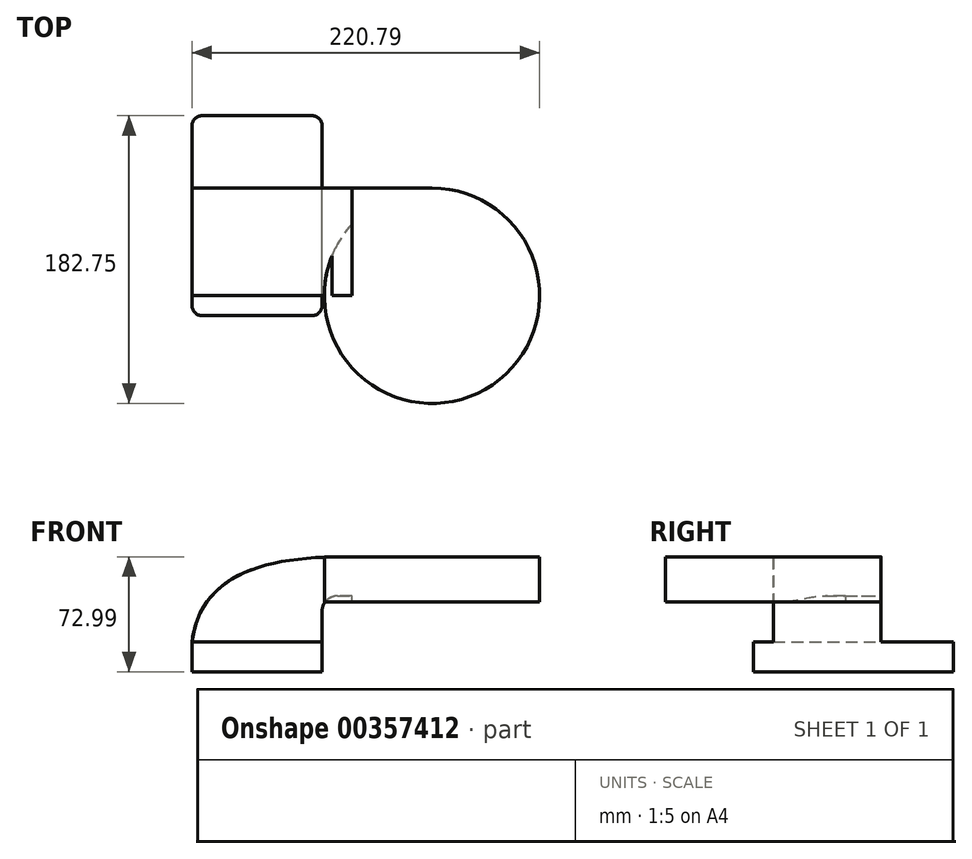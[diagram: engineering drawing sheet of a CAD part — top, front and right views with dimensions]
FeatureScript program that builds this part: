
annotation { "Feature Type Name" : "Feature", "Feature Type Description" : "" }
export const myFeature = defineFeature(function(context is Context, id is Id, definition is map)
    precondition{}
    {
        {
            var Q0;
            Q0=qCreatedBy(makeId("Front.planeOp"),FACE);
            var sketch = newSketch(context, id + "F0", { "sketchPlane" : qUnion([Q0])});
            skLineSegment(sketch, "E0.bottom", {"start": v(41.28, -9.52) * mm, "end": v(-41.28, -9.53) * mm});
            skLineSegment(sketch, "E0.top", {"start": v(41.28, 9.53) * mm, "end": v(-41.28, 9.53) * mm});
            skLineSegment(sketch, "E0.left", {"start": v(41.28, -9.52) * mm, "end": v(41.28, 9.53) * mm});
            skLineSegment(sketch, "E0.right", {"start": v(-41.28, -9.53) * mm, "end": v(-41.28, 9.53) * mm});
            skPoint(sketch, "E0.middle", {"position": v(0, 0) * mm});
            skLineSegment(sketch, "E1.bottom", {"start": v(60.33, 34.82) * mm, "end": v(111.12, 34.82) * mm});
            skLineSegment(sketch, "E1.top", {"start": v(60.33, 63.4) * mm, "end": v(111.12, 63.4) * mm});
            skLineSegment(sketch, "E1.left", {"start": v(60.33, 34.82) * mm, "end": v(60.33, 63.4) * mm});
            skLineSegment(sketch, "E1.right", {"start": v(111.12, 34.82) * mm, "end": v(111.12, 63.4) * mm});
            skPoint(sketch, "E1.middle", {"position": v(85.72, 49.11) * mm});
            skLineSegment(sketch, "E2", {"start": v(41.28, 9.53) * mm, "end": v(41.28, 28.87) * mm});
            skArc(sketch, "E3", {"start": v(41.28, 28.87) * mm, "mid": v(44.18, 35.9) * mm, "end": v(51.2, 38.8) * mm});
            skLineSegment(sketch, "E4", {"start": v(51.2, 38.8) * mm, "end": v(103.6, 38.8) * mm});
            skArc(sketch, "E5.0", {"start": v(22.23, 28.87) * mm, "mid": v(30.71, 49.37) * mm, "end": v(51.2, 57.85) * mm});
            skLineSegment(sketch, "E6", {"start": v(22.23, 28.87) * mm, "end": v(22.23, 9.53) * mm});
            skLineSegment(sketch, "E7", {"start": v(51.2, 57.85) * mm, "end": v(103.6, 57.85) * mm});
            skLineSegment(sketch, "E8", {"start": v(85.72, 34.82) * mm, "end": v(85.72, 63.4) * mm});
            skFitSpline(sketch, "E9", {"points": [v(-41.28, 9.53) * mm, v(60.33, 63.4) * mm], "startDerivative": vector(16.64, 133.57) * mm, "endDerivative": vector(155.6, -3) * mm});
            skSolve(sketch);
        }
        {
            var Q0;
            Q0=makeQuery(id+"F0.imprint","IMPRINT",FACE,{"disambiguationData":[TD([[makeQuery(id+"F0.imprint","IMPRINT",EDGE,{"derivedFrom":sQuery(id+"F0.wireOp",EDGE,"E0.bottom")}),-1.0]])]});
            extrude(context, id + "F1", {"entities" : qUnion([Q0]), "endBound" : BoundingType.SYMMETRIC, "depth" : 127 * mm});
        }
        {
            var Q0;
            Q0 = qSketchRegion(id + "F0", true);
            extrude(context, id + "F2", {"entities" : qUnion([Q0]), "operationType" : NewBodyOperationType.ADD, "endBound" : BoundingType.SYMMETRIC, "depth" : 35.05 * mm});
        }
        {
            var Q0;
            Q0=makeQuery(id+"F2.opExtrude","CAP_FACE",FACE,{"disambiguationData":[OSD([sQuery(id+"F0.wireOp",EDGE,"E0.bottom"),sQuery(id+"F0.wireOp",EDGE,"E0.left"),sQuery(id+"F0.wireOp",EDGE,"E0.right"),sQuery(id+"F0.wireOp",EDGE,"E1.bottom"),sQuery(id+"F0.wireOp",EDGE,"E1.top"),sQuery(id+"F0.wireOp",EDGE,"E1.left"),sQuery(id+"F0.wireOp",EDGE,"E1.right"),sQuery(id+"F0.wireOp",EDGE,"E2"),sQuery(id+"F0.wireOp",EDGE,"E3"),sQuery(id+"F0.wireOp",EDGE,"E4"),sQuery(id+"F0.wireOp",EDGE,"E9")])],"isStart":false});
            extrude(context, id + "F3", {"entities" : qUnion([Q0]), "operationType" : NewBodyOperationType.ADD, "endBound" : BoundingType.SYMMETRIC, "depth" : 50.8 * mm});
        }
        {
            var Q0;
            Q0=makeQuery(id+"F3.opExtrude","CAP_FACE",FACE,{"disambiguationData":[OSD([sQuery(id+"F0.wireOp",EDGE,"E0.bottom"),sQuery(id+"F0.wireOp",EDGE,"E0.left"),sQuery(id+"F0.wireOp",EDGE,"E0.right"),sQuery(id+"F0.wireOp",EDGE,"E1.bottom"),sQuery(id+"F0.wireOp",EDGE,"E1.top"),sQuery(id+"F0.wireOp",EDGE,"E1.left"),sQuery(id+"F0.wireOp",EDGE,"E1.right"),sQuery(id+"F0.wireOp",EDGE,"E2"),sQuery(id+"F0.wireOp",EDGE,"E3"),sQuery(id+"F0.wireOp",EDGE,"E4"),sQuery(id+"F0.wireOp",EDGE,"E9")])],"isStart":false});
            extrude(context, id + "F4", {"entities" : qUnion([Q0]), "operationType" : NewBodyOperationType.ADD, "endBound" : BoundingType.SYMMETRIC, "depth" : 15.88 * mm});
        }
        {
            var Q0;
            {var subQ0=sQuery(id+"F0.wireOp",EDGE,"E1.right");Q0=makeQuery(id+"F4.boolean.opBoolean","MERGE",FACE,{"derivedFrom":[makeQuery(id+"F3.boolean.opBoolean","MERGE",FACE,{"derivedFrom":[makeQuery(id+"F2.opExtrude","SWEPT_FACE",FACE,{"disambiguationData":[OSD([subQ0])]}),makeQuery(id+"F3.opExtrude","SWEPT_FACE",FACE,{"disambiguationData":[OSD([subQ0])]})]}),makeQuery(id+"F4.opExtrude","SWEPT_FACE",FACE,{"disambiguationData":[OSD([subQ0])]})]});}
            var Q1;
            Q1=makeQuery(id+"F4.opExtrude","CAP_EDGE",EDGE,{"disambiguationData":[OSD([sQuery(id+"F0.wireOp",EDGE,"E1.right")])],"isStart":false});
            revolve(context, id + "F5", {"operationType" : NewBodyOperationType.ADD, "entities" : qUnion([Q0]), "axis" : qUnion([Q1]), "revolveType" : RevolveType.FULL});
        }
        {
            var Q0;
            Q0=makeQuery(id+"F1.opExtrude","CAP_EDGE",EDGE,{"disambiguationData":[OSD([sQuery(id+"F0.wireOp",EDGE,"E0.right")])],"isStart":false});
            var Q1;
            Q1=makeQuery(id+"F1.opExtrude","CAP_EDGE",EDGE,{"disambiguationData":[OSD([sQuery(id+"F0.wireOp",EDGE,"E0.left")])],"isStart":false});
            var Q2;
            Q2=makeQuery(id+"F1.opExtrude","CAP_EDGE",EDGE,{"disambiguationData":[OSD([sQuery(id+"F0.wireOp",EDGE,"E0.left")])],"isStart":true});
            var Q3;
            Q3=makeQuery(id+"F1.opExtrude","CAP_EDGE",EDGE,{"disambiguationData":[OSD([sQuery(id+"F0.wireOp",EDGE,"E0.right")])],"isStart":true});
            fillet(context, id + "F6", {"entities" : qUnion([Q0, Q1, Q2, Q3]), "radius" : 6.35 * mm, "tangentPropagation" : true, "allowEdgeOverflow" : false});
        }
    });
